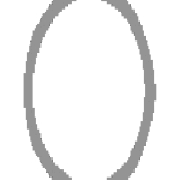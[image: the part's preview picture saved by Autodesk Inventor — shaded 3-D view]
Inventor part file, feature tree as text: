
AUTODESK INVENTOR PART (.ipt)
format: ipt  version: 2021 (Build 250183000, 183)  size: 112,128 bytes
history: native  units: in
note: dims shown in document units (in); Inventor stores cm internally (conversion verified against a paired STEP export)
features: other x4, sketch x3, plane x1
ambient origin geometry x8: Origin, YZ Plane, XZ Plane, XY Plane, X Axis, Y Axis, Z Axis, Center Point
bodies: Solid1 (feature_tree), Body (feature_tree)
feature tree (8):
  other  "Driven Length"
  other  "Frame Generator"
  other  "Start Plane"
  other  "End Plane"
  sketch  "Sketch"  dims[d2=6.7082in d4=-0.0in d5=6.7082in d6=0.12in d7=0.0in d10=90.0deg d9=6.7082in]
  sketch  "Sketch4"  dims[d0=1.0in]
  plane  "Work Plane4"
  sketch  "Sketch5"  dims[d1=0.065in]
